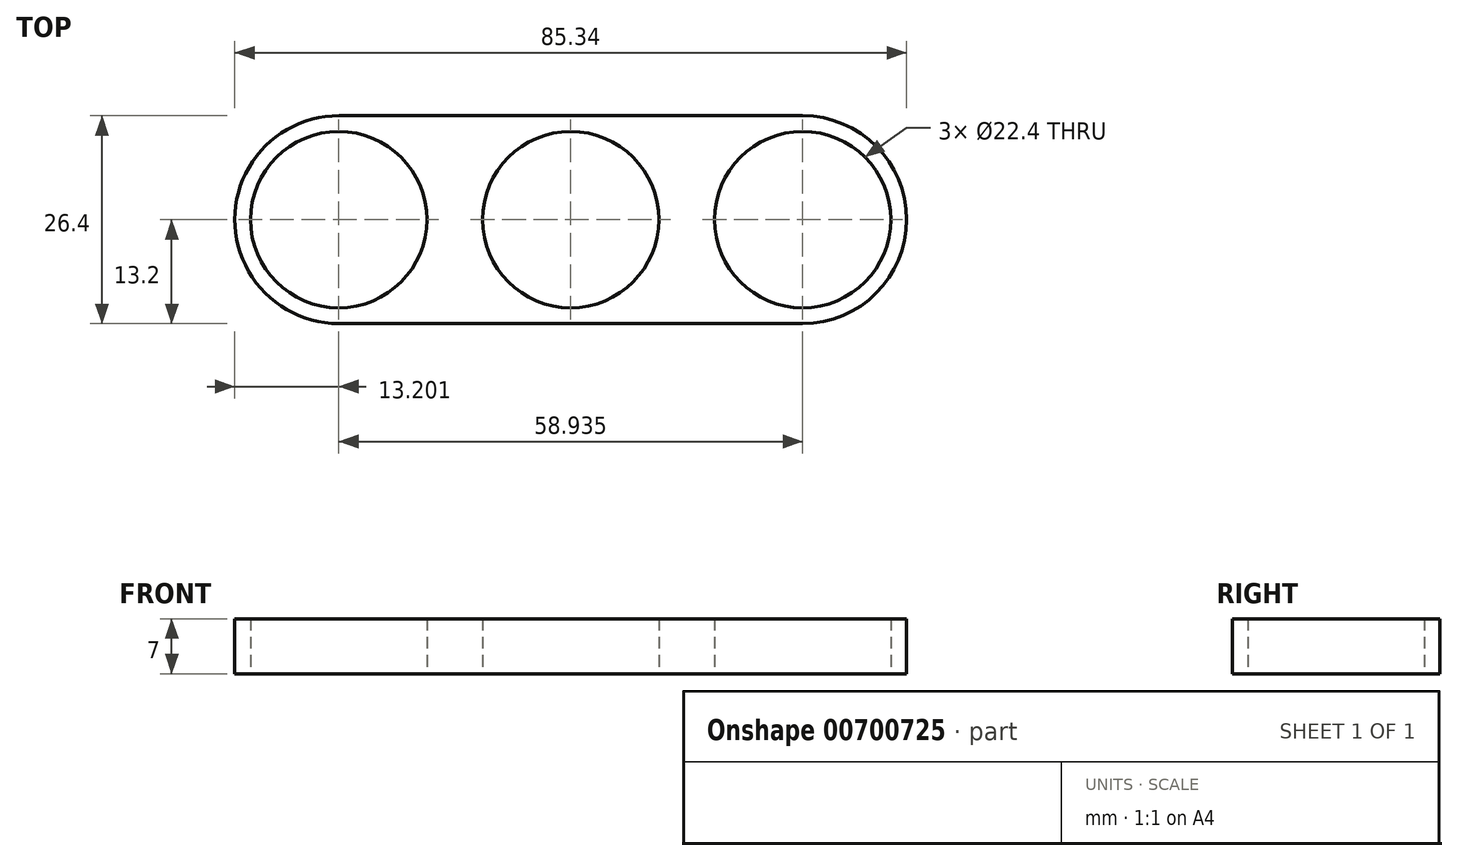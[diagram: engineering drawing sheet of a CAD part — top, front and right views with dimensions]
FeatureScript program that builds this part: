
annotation { "Feature Type Name" : "Feature", "Feature Type Description" : "" }
export const myFeature = defineFeature(function(context is Context, id is Id, definition is map)
    precondition{}
    {
        {
            var Q0;
            Q0=qCreatedBy(makeId("Top.planeOp"),FACE);
            var sketch = newSketch(context, id + "F0", { "sketchPlane" : qUnion([Q0])});
            skCircle(sketch, "E0", {"center": v(0, 0) * mm, "radius": 11.2 * mm});
            skCircle(sketch, "E1", {"center": v(0, 0) * mm, "radius": 13.2 * mm});
            skCircle(sketch, "E2", {"center": v(-29.47, 0) * mm, "radius": 11.2 * mm});
            skArc(sketch, "E3", {"start": v(-29.44, 13.2) * mm, "mid": v(-42.67, 0) * mm, "end": v(-29.44, -13.2) * mm});
            skArc(sketch, "E4.1.0", {"start": v(29.47, -13.2) * mm, "mid": v(42.67, 0) * mm, "end": v(29.47, 13.2) * mm});
            skCircle(sketch, "E4.1.1", {"center": v(29.47, 0) * mm, "radius": 11.2 * mm});
            skLineSegment(sketch, "E5", {"start": v(-29.44, 13.2) * mm, "end": v(29.47, 13.2) * mm});
            skLineSegment(sketch, "E6", {"start": v(-29.5, -13.2) * mm, "end": v(29.47, -13.2) * mm});
            skSolve(sketch);
        }
        {
            var Q0;
            Q0=makeQuery(id+"F0.imprint","IMPRINT",FACE,{"disambiguationData":[TD([[makeQuery(id+"F0.imprint","IMPRINT",EDGE,{"derivedFrom":sQuery(id+"F0.wireOp",EDGE,"E2")}),-1.0]])]});
            var Q1;
            {var subQ1=sQuery(id+"F0.wireOp",EDGE,"E4.1.0");Q1=makeQuery(id+"F0.imprint","IMPRINT",FACE,{"disambiguationData":[TD([[makeQuery(id+"F0.imprint","IMPRINT",EDGE,{"derivedFrom":subQ1}),1.0]])]});}
            var Q2;
            Q2=makeQuery(id+"F0.imprint","IMPRINT",FACE,{"disambiguationData":[TD([[makeQuery(id+"F0.imprint","IMPRINT",EDGE,{"derivedFrom":sQuery(id+"F0.wireOp",EDGE,"E0")}),-1.0]])]});
            extrude(context, id + "F1", {"entities" : qUnion([Q0, Q1, Q2]), "depth" : 7 * mm, "offsetDistance" : 25 * mm});
        }
    });
